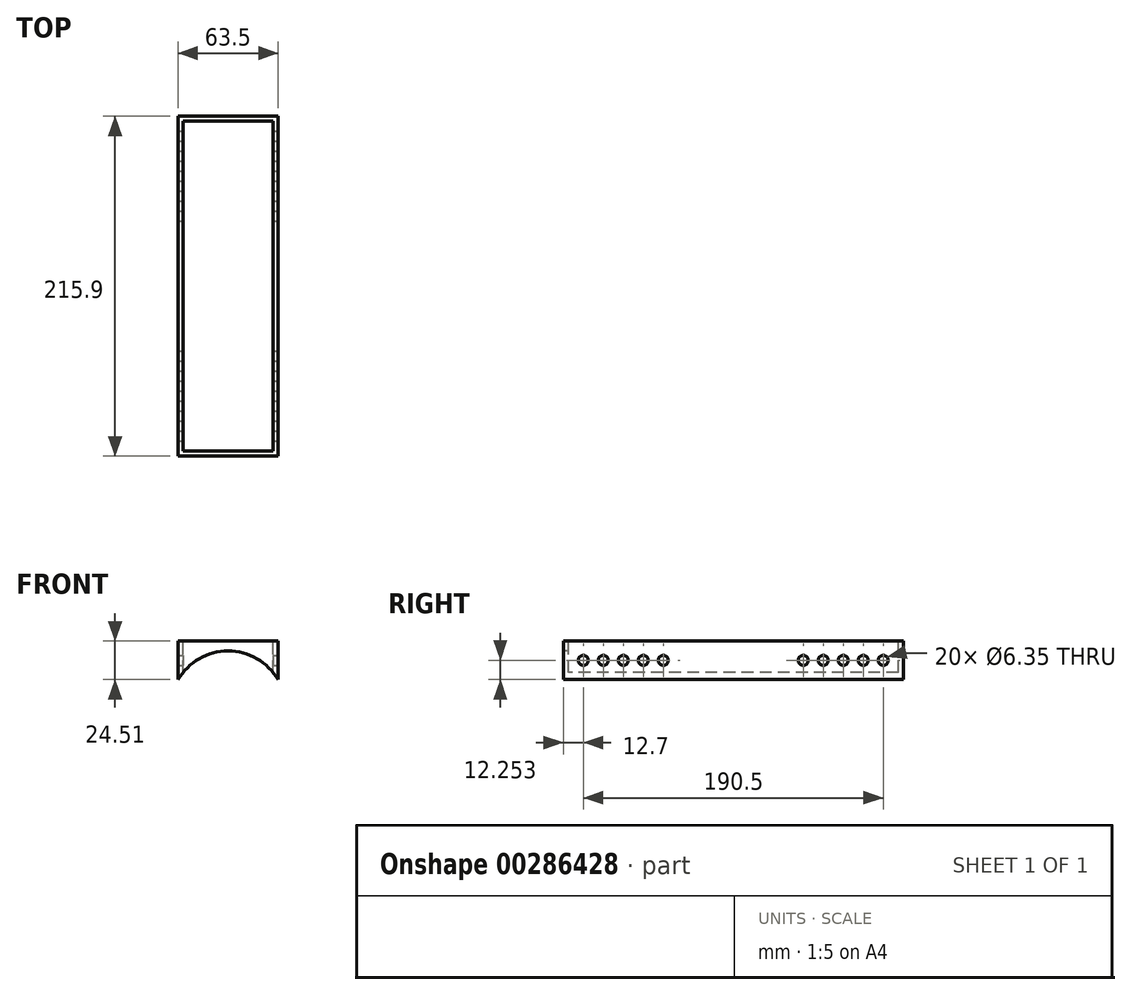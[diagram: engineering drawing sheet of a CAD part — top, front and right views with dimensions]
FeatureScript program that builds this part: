
annotation { "Feature Type Name" : "Feature", "Feature Type Description" : "" }
export const myFeature = defineFeature(function(context is Context, id is Id, definition is map)
    precondition{}
    {
        {
            var Q0;
            Q0=qCreatedBy(makeId("Front.planeOp"),FACE);
            var sketch = newSketch(context, id + "F0", { "sketchPlane" : qUnion([Q0])});
            skArc(sketch, "E0", {"start": v(-30.48, 0) * mm, "mid": v(0, 30.48) * mm, "end": v(30.48, 0) * mm});
            skArc(sketch, "E1.0", {"start": v(-36.28, 6.35) * mm, "mid": v(0, 36.83) * mm, "end": v(36.28, 6.35) * mm});
            skLineSegment(sketch, "E2", {"start": v(30.48, 0) * mm, "end": v(36.83, 0) * mm});
            skLineSegment(sketch, "E3", {"start": v(-36.83, 0) * mm, "end": v(-30.48, 0) * mm});
            skLineSegment(sketch, "E4", {"start": v(0, 36.83) * mm, "end": v(0, 43.18) * mm, "construction": true});
            skPoint(sketch, "E4.endSnap0", {"position": v(0, 36.83) * mm});
            skLineSegment(sketch, "E5", {"start": v(-28.58, 43.18) * mm, "end": v(28.57, 43.18) * mm});
            skLineSegment(sketch, "E6", {"start": v(28.58, 43.18) * mm, "end": v(28.58, 23.24) * mm});
            skLineSegment(sketch, "E7", {"start": v(-28.58, 43.18) * mm, "end": v(-28.58, 23.24) * mm});
            skLineSegment(sketch, "E8", {"start": v(28.57, 43.18) * mm, "end": v(31.75, 43.18) * mm});
            skLineSegment(sketch, "E9", {"start": v(-28.58, 43.18) * mm, "end": v(-31.75, 43.18) * mm});
            skLineSegment(sketch, "E10", {"start": v(-31.75, 43.18) * mm, "end": v(-31.75, 18.67) * mm});
            skLineSegment(sketch, "E11", {"start": v(31.75, 43.18) * mm, "end": v(31.75, 18.67) * mm});
            skLineSegment(sketch, "E12", {"start": v(36.83, 0) * mm, "end": v(49.53, 0) * mm});
            skLineSegment(sketch, "E13", {"start": v(49.53, 0) * mm, "end": v(49.53, 6.35) * mm});
            skLineSegment(sketch, "E14", {"start": v(-36.83, 0) * mm, "end": v(-49.53, 0) * mm});
            skLineSegment(sketch, "E15", {"start": v(-49.53, 0) * mm, "end": v(-49.53, 6.35) * mm});
            skLineSegment(sketch, "E16", {"start": v(-49.53, 6.35) * mm, "end": v(-36.28, 6.35) * mm});
            skLineSegment(sketch, "E17", {"start": v(49.53, 6.35) * mm, "end": v(36.28, 6.35) * mm});
            skSolve(sketch);
        }
        {
            var Q0;
            Q0=makeQuery(id+"F0.imprint","IMPRINT",FACE,{"disambiguationData":[TD([[makeQuery(id+"F0.imprint","IMPRINT",EDGE,{"derivedFrom":sQuery(id+"F0.wireOp",EDGE,"E0")}),1.0]])]});
            var Q1;
            {var subQ0=sQuery(id+"F0.wireOp",EDGE,"E6");Q1=makeQuery(id+"F0.imprint","IMPRINT",FACE,{"disambiguationData":[TD([[makeQuery(id+"F0.imprint","IMPRINT",EDGE,{"derivedFrom":subQ0}),1.0]])]});}
            var Q2;
            Q2=makeQuery(id+"F0.imprint","IMPRINT",FACE,{"disambiguationData":[TD([[makeQuery(id+"F0.imprint","IMPRINT",EDGE,{"derivedFrom":sQuery(id+"F0.wireOp",EDGE,"E5")}),-1.0]])]});
            var Q3;
            {var subQ0=sQuery(id+"F0.wireOp",EDGE,"E7");Q3=makeQuery(id+"F0.imprint","IMPRINT",FACE,{"disambiguationData":[TD([[makeQuery(id+"F0.imprint","IMPRINT",EDGE,{"derivedFrom":subQ0}),-1.0]])]});}
            extrude(context, id + "F1", {"entities" : qUnion([Q0, Q1, Q2, Q3]), "oppositeDirection" : true, "depth" : 215.9 * mm});
        }
        {
            var Q0;
            Q0=makeQuery(id+"F1.opExtrude","SWEPT_FACE",FACE,{"disambiguationData":[OSD([sQuery(id+"F0.wireOp",EDGE,"E5"),sQuery(id+"F0.wireOp",EDGE,"E8"),sQuery(id+"F0.wireOp",EDGE,"E9")])]});
            var sketch = newSketch(context, id + "F2", { "sketchPlane" : qUnion([Q0])});
            skLineSegment(sketch, "E18.0", {"start": v(-28.58, 212.72) * mm, "end": v(-28.58, 3.18) * mm});
            skLineSegment(sketch, "E18.1", {"start": v(-28.58, 212.72) * mm, "end": v(28.58, 212.72) * mm});
            skLineSegment(sketch, "E18.2", {"start": v(28.58, 212.72) * mm, "end": v(28.58, 3.18) * mm});
            skLineSegment(sketch, "E18.3", {"start": v(-28.58, 3.18) * mm, "end": v(28.58, 3.18) * mm});
            skSolve(sketch);
        }
        {
            var Q0;
            Q0=makeQuery(id+"F2.imprint","IMPRINT",FACE,{"disambiguationData":[TD([[makeQuery(id+"F2.imprint","IMPRINT",EDGE,{"derivedFrom":sQuery(id+"F2.wireOp",EDGE,"E18.0")}),1.0]])]});
            extrude(context, id + "F3", {"entities" : qUnion([Q0]), "operationType" : NewBodyOperationType.REMOVE, "endBound" : BoundingType.UP_TO_NEXT, "oppositeDirection" : true, "depth" : 25.4 * mm});
        }
        {
            var Q0;
            Q0=makeQuery(id+"F1.opExtrude","SWEPT_FACE",FACE,{"disambiguationData":[OSD([sQuery(id+"F0.wireOp",EDGE,"E11")])]});
            var sketch = newSketch(context, id + "F4", { "sketchPlane" : qUnion([Q0])});
            skPoint(sketch, "E19.0", {"position": v(0, 30.92) * mm});
            skPoint(sketch, "E20.0", {"position": v(215.9, 30.92) * mm});
            skLineSegment(sketch, "E21", {"start": v(0, 30.92) * mm, "end": v(12.7, 30.92) * mm, "construction": true});
            skLineSegment(sketch, "E22", {"start": v(12.7, 30.92) * mm, "end": v(25.4, 30.92) * mm, "construction": true});
            skLineSegment(sketch, "E23", {"start": v(25.4, 30.92) * mm, "end": v(38.1, 30.92) * mm, "construction": true});
            skLineSegment(sketch, "E24", {"start": v(38.1, 30.92) * mm, "end": v(50.8, 30.92) * mm, "construction": true});
            skLineSegment(sketch, "E25", {"start": v(50.8, 30.92) * mm, "end": v(63.5, 30.92) * mm, "construction": true});
            skLineSegment(sketch, "E26", {"start": v(63.5, 30.92) * mm, "end": v(76.2, 30.92) * mm, "construction": true});
            skLineSegment(sketch, "E27", {"start": v(76.2, 30.92) * mm, "end": v(88.9, 30.92) * mm, "construction": true});
            skLineSegment(sketch, "E28", {"start": v(88.9, 30.92) * mm, "end": v(101.6, 30.92) * mm, "construction": true});
            skLineSegment(sketch, "E29", {"start": v(101.6, 30.92) * mm, "end": v(114.3, 30.92) * mm, "construction": true});
            skLineSegment(sketch, "E30", {"start": v(114.3, 30.92) * mm, "end": v(127, 30.92) * mm, "construction": true});
            skLineSegment(sketch, "E31", {"start": v(127, 30.92) * mm, "end": v(139.7, 30.92) * mm, "construction": true});
            skLineSegment(sketch, "E32", {"start": v(139.7, 30.92) * mm, "end": v(152.4, 30.92) * mm, "construction": true});
            skLineSegment(sketch, "E33", {"start": v(152.4, 30.92) * mm, "end": v(165.1, 30.92) * mm, "construction": true});
            skLineSegment(sketch, "E34", {"start": v(165.1, 30.92) * mm, "end": v(177.8, 30.92) * mm, "construction": true});
            skLineSegment(sketch, "E35", {"start": v(177.8, 30.92) * mm, "end": v(190.5, 30.92) * mm, "construction": true});
            skLineSegment(sketch, "E36", {"start": v(190.5, 30.92) * mm, "end": v(203.2, 30.92) * mm, "construction": true});
            skLineSegment(sketch, "E37", {"start": v(203.2, 30.92) * mm, "end": v(215.9, 30.92) * mm, "construction": true});
            skCircle(sketch, "E38", {"center": v(12.7, 30.92) * mm, "radius": 3.18 * mm});
            skCircle(sketch, "E39", {"center": v(25.4, 30.92) * mm, "radius": 3.18 * mm});
            skCircle(sketch, "E40", {"center": v(38.1, 30.92) * mm, "radius": 3.18 * mm});
            skCircle(sketch, "E41", {"center": v(50.8, 30.92) * mm, "radius": 3.18 * mm});
            skCircle(sketch, "E42", {"center": v(63.5, 30.92) * mm, "radius": 3.18 * mm});
            skCircle(sketch, "E43", {"center": v(152.4, 30.92) * mm, "radius": 3.18 * mm});
            skCircle(sketch, "E44", {"center": v(165.1, 30.92) * mm, "radius": 3.18 * mm});
            skCircle(sketch, "E45", {"center": v(177.8, 30.92) * mm, "radius": 3.18 * mm});
            skCircle(sketch, "E46", {"center": v(190.5, 30.92) * mm, "radius": 3.18 * mm});
            skCircle(sketch, "E47", {"center": v(203.2, 30.92) * mm, "radius": 3.18 * mm});
            skSolve(sketch);
        }
        {
            var Q0;
            Q0=makeQuery(id+"F4.imprint","IMPRINT",FACE,{"disambiguationData":[TD([[makeQuery(id+"F4.imprint","IMPRINT",EDGE,{"derivedFrom":sQuery(id+"F4.wireOp",EDGE,"E38")}),1.0]])]});
            var Q1;
            Q1=makeQuery(id+"F4.imprint","IMPRINT",FACE,{"disambiguationData":[TD([[makeQuery(id+"F4.imprint","IMPRINT",EDGE,{"derivedFrom":sQuery(id+"F4.wireOp",EDGE,"E39")}),1.0]])]});
            var Q2;
            Q2=makeQuery(id+"F4.imprint","IMPRINT",FACE,{"disambiguationData":[TD([[makeQuery(id+"F4.imprint","IMPRINT",EDGE,{"derivedFrom":sQuery(id+"F4.wireOp",EDGE,"E40")}),1.0]])]});
            var Q3;
            Q3=makeQuery(id+"F4.imprint","IMPRINT",FACE,{"disambiguationData":[TD([[makeQuery(id+"F4.imprint","IMPRINT",EDGE,{"derivedFrom":sQuery(id+"F4.wireOp",EDGE,"E41")}),1.0]])]});
            var Q4;
            Q4=makeQuery(id+"F4.imprint","IMPRINT",FACE,{"disambiguationData":[TD([[makeQuery(id+"F4.imprint","IMPRINT",EDGE,{"derivedFrom":sQuery(id+"F4.wireOp",EDGE,"E42")}),1.0]])]});
            var Q5;
            Q5=makeQuery(id+"F4.imprint","IMPRINT",FACE,{"disambiguationData":[TD([[makeQuery(id+"F4.imprint","IMPRINT",EDGE,{"derivedFrom":sQuery(id+"F4.wireOp",EDGE,"v5FU449B-lqfH-wZE0-w72f-SDNpIDD7x22d")}),1.0]])]});
            var Q6;
            Q6=makeQuery(id+"F4.imprint","IMPRINT",FACE,{"disambiguationData":[TD([[makeQuery(id+"F4.imprint","IMPRINT",EDGE,{"derivedFrom":sQuery(id+"F4.wireOp",EDGE,"ujCConix-R9uu-su5w-bRI8-uIZPEh9RfC6D")}),1.0]])]});
            var Q7;
            Q7=makeQuery(id+"F4.imprint","IMPRINT",FACE,{"disambiguationData":[TD([[makeQuery(id+"F4.imprint","IMPRINT",EDGE,{"derivedFrom":sQuery(id+"F4.wireOp",EDGE,"OthDsbow-v0h5-lAiX-QpJx-ajvZiV48msnr")}),1.0]])]});
            var Q8;
            Q8=makeQuery(id+"F4.imprint","IMPRINT",FACE,{"disambiguationData":[TD([[makeQuery(id+"F4.imprint","IMPRINT",EDGE,{"derivedFrom":sQuery(id+"F4.wireOp",EDGE,"toIDYhwN-jzo4-28sN-Zwko-6HCt2DrBb24r")}),1.0]])]});
            var Q9;
            Q9=makeQuery(id+"F4.imprint","IMPRINT",FACE,{"disambiguationData":[TD([[makeQuery(id+"F4.imprint","IMPRINT",EDGE,{"derivedFrom":sQuery(id+"F4.wireOp",EDGE,"0TrdL7eo-0ub8-sOd1-FT3J-DAuRasmWlURw")}),1.0]])]});
            var Q10;
            Q10=makeQuery(id+"F4.imprint","IMPRINT",FACE,{"disambiguationData":[TD([[makeQuery(id+"F4.imprint","IMPRINT",EDGE,{"derivedFrom":sQuery(id+"F4.wireOp",EDGE,"mtStiGUj-00fl-s94U-zQ5o-hq3WJnlgCYEl")}),1.0]])]});
            var Q11;
            Q11=makeQuery(id+"F4.imprint","IMPRINT",FACE,{"disambiguationData":[TD([[makeQuery(id+"F4.imprint","IMPRINT",EDGE,{"derivedFrom":sQuery(id+"F4.wireOp",EDGE,"E43")}),1.0]])]});
            var Q12;
            Q12=makeQuery(id+"F4.imprint","IMPRINT",FACE,{"disambiguationData":[TD([[makeQuery(id+"F4.imprint","IMPRINT",EDGE,{"derivedFrom":sQuery(id+"F4.wireOp",EDGE,"E44")}),1.0]])]});
            var Q13;
            Q13=makeQuery(id+"F4.imprint","IMPRINT",FACE,{"disambiguationData":[TD([[makeQuery(id+"F4.imprint","IMPRINT",EDGE,{"derivedFrom":sQuery(id+"F4.wireOp",EDGE,"E45")}),1.0]])]});
            var Q14;
            Q14=makeQuery(id+"F4.imprint","IMPRINT",FACE,{"disambiguationData":[TD([[makeQuery(id+"F4.imprint","IMPRINT",EDGE,{"derivedFrom":sQuery(id+"F4.wireOp",EDGE,"E46")}),1.0]])]});
            var Q15;
            Q15=makeQuery(id+"F4.imprint","IMPRINT",FACE,{"disambiguationData":[TD([[makeQuery(id+"F4.imprint","IMPRINT",EDGE,{"derivedFrom":sQuery(id+"F4.wireOp",EDGE,"E47")}),1.0]])]});
            extrude(context, id + "F5", {"entities" : qUnion([Q0, Q1, Q2, Q3, Q4, Q5, Q6, Q7, Q8, Q9, Q10, Q11, Q12, Q13, Q14, Q15]), "operationType" : NewBodyOperationType.REMOVE, "endBound" : BoundingType.THROUGH_ALL, "oppositeDirection" : true, "depth" : 25.4 * mm});
        }
    });
